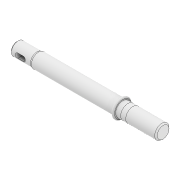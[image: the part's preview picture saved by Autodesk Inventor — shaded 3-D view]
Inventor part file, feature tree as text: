
AUTODESK INVENTOR PART (.ipt)
format: ipt  version: 2022 (Build 260153000, 153)  size: 183,296 bytes
history: native  units: mm
features: extrude x5, sketch x5, plane x2, fillet x2, projected_geometry x2, other x2, loft x1, chamfer x1
ambient origin geometry x8: Origin, YZ Plane, XZ Plane, XY Plane, X Axis, Y Axis, Z Axis, Center Point
bodies: Solid1 (feature_tree)
feature tree (20):
  extrude  "Shaft"  Depth=2.35mm TaperAngle=0.0deg
  extrude  "Slot for Differential Gear"  Depth=2.0mm
  plane  "Work Plane1"
  extrude  "Wheel Insert Profile"  Depth=7.0mm
  loft  "Loft1"
  plane  "Work Plane2"
  extrude  "Stopper"  Depth=7.5mm
  fillet  "Fillet1"  Radius=1.0mm
  extrude  "Differential Gear Insert Profile"  Depth=0.5mm
  fillet  "Fillet3"  Radius=3.0mm
  chamfer  "Chamfer4"  Distance=2.5mm
  sketch  "Sketch1"  dims[d2=0.0mm d9=2.35mm d10=0.0mm]
  sketch  "Sketch2"  dims[d17=1.8mm d20=2.0mm]
  sketch  "Sketch3"  dims[d21=1.0mm d22=7.0mm]
  sketch  "Sketch4"  dims[d25=12.0mm d26=0.0mm d29=2.0mm d32=0.0mm d33=90.0deg]
  projected_geometry  "Projected Loop1"
  other  "Edges2"
  other  "Edges4"
  sketch  "Sketch8"  dims[d34=-41.0mm d35=7.5mm d36=1.0mm d37=0.0mm d38=0.5mm d49=3.0mm d50=2.5mm d62=0.0mm d63=90.0deg d68=5.4mm d69=0.05mm d70=8.0mm d71=0.0mm d72=1.0mm d73=0.5mm d74=2.0mm d75=45.0deg]
  projected_geometry  "Project Cut Edges1"
